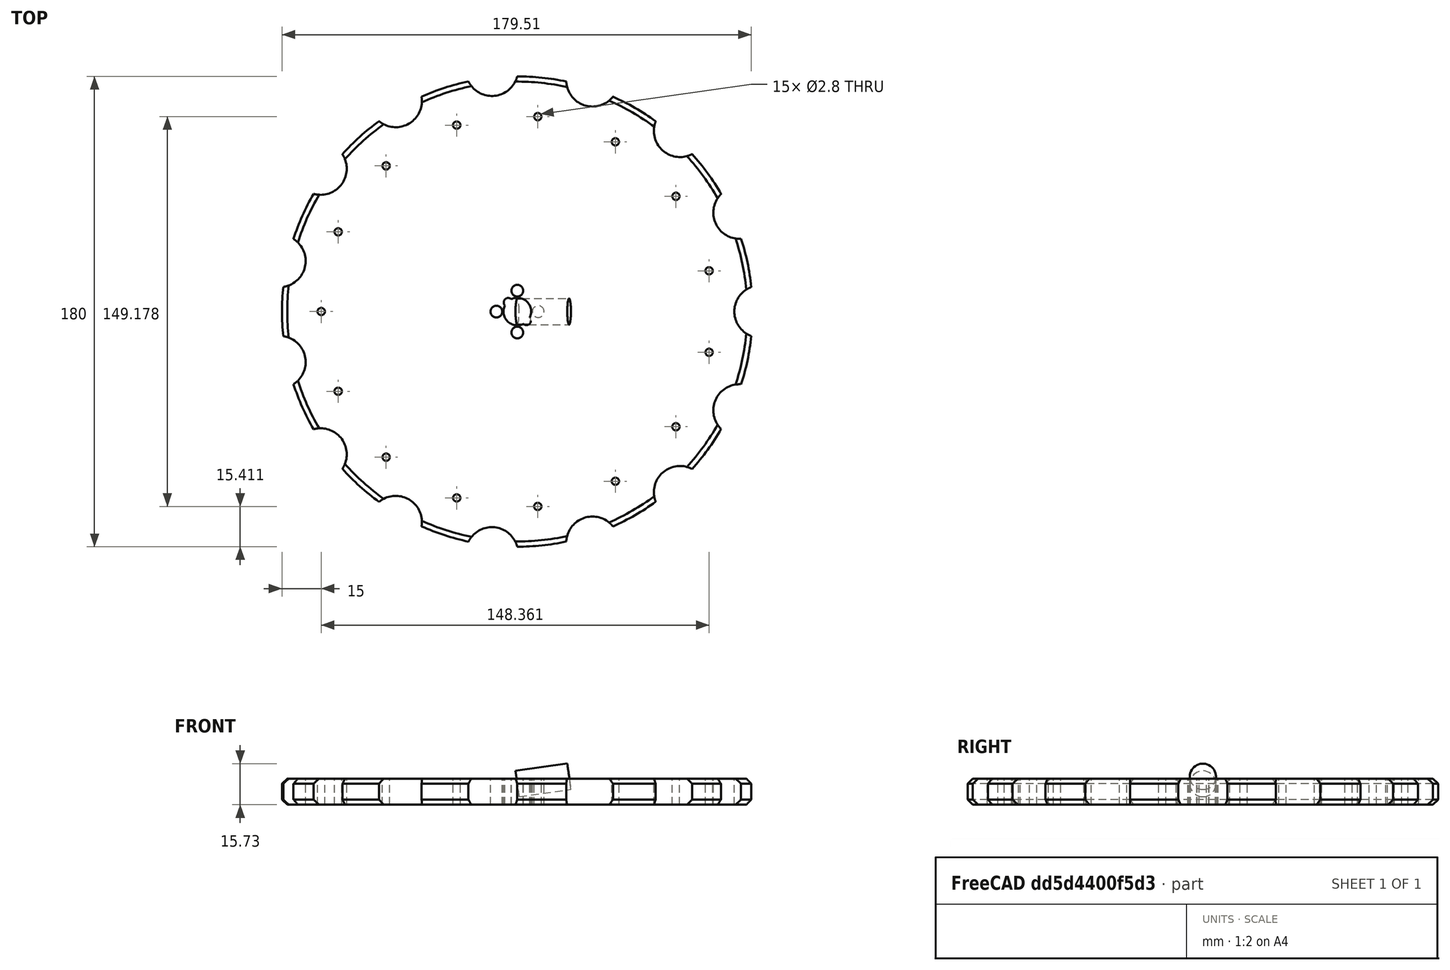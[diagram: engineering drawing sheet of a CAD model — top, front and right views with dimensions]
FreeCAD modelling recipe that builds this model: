
FCSTD DOCUMENT  (FreeCAD 0.17R13541 (Git))
Label: rueda180mmeje
License: All rights reserved
LicenseURL: http://en.wikipedia.org/wiki/All_rights_reserved
objects: Part::Cylinder×8, Part::FeaturePython×3, Part::Cut×3, Part::Chamfer×1, Part::MultiFuse×1
note: 16 computed .brp shape members not serialized (recipe doc carries the construction recipe); baked Part::Feature solids carry a one-line shape summary decoded from their .brp

FEATURE [Part::Cylinder] Cylinder  label="Cilindro"
  Angle = 360
  AttacherType = Attacher::AttachEngine3D
  Height = 10
  Radius = 90
FEATURE [Part::Chamfer] Chamfer
  Base = -> Cylinder
  Edges = 2 edges r=2: [Edge1,Edge3]
FEATURE [Part::Cylinder] Cylinder001  label="Cilindro001"
  Angle = 360
  AttacherType = Attacher::AttachEngine3D
  Height = 15
  Placement = pos=(93,0,0) rot=(0,0,1;0rad)
  Radius = 10
FEATURE [Part::FeaturePython] Array  # Draft array (typed FeaturePython)
  Angle = 360
  ArrayType = 1
  Axis = (0,0,1)
  Base = -> Cylinder001
  Center = (0,0,0)
  Fuse = false
  IntervalAxis = (0,0,0)
  IntervalX = (1,0,0)
  IntervalY = (0,1,0)
  IntervalZ = (0,0,0)
  NumberPolar = 15
  NumberX = 2
  NumberY = 2
  NumberZ = 1
FEATURE [Part::Cylinder] Cylinder004  label="Cilindro004"
  Angle = 360
  AttacherType = Attacher::AttachEngine3D
  Height = 20
  Placement = pos=(0,0,8) rot=(0,1,0;1.43117rad)
  Radius = 5
FEATURE [Part::Cylinder] Cylinder006  label="Cilindro006"
  Angle = 360
  AttacherType = Attacher::AttachEngine3D
  Height = 12
  Placement = pos=(-75,0,0) rot=(0,0,1;0rad)
  Radius = 1.4
FEATURE [Part::FeaturePython] Array001  # Draft array (typed FeaturePython)
  Angle = 360
  ArrayType = 1
  Axis = (0,0,1)
  Base = -> Cylinder006
  Center = (0,0,0)
  Fuse = false
  IntervalAxis = (0,0,0)
  IntervalX = (1,0,0)
  IntervalY = (0,1,0)
  IntervalZ = (0,0,0)
  NumberPolar = 15
  NumberX = 2
  NumberY = 2
  NumberZ = 1
FEATURE [Part::Cut] Cut
  Base = -> Chamfer
  Refine = true
  Tool = -> Array
FEATURE [Part::Cut] Cut001
  Base = -> Cut
  Refine = true
  Tool = -> Array001
FEATURE [Part::Cylinder] Cylinder007  label="Cilindro002"
  Angle = 360
  AttacherType = Attacher::AttachEngine3D
  Height = 15
  Placement = pos=(3.5,-3.5,0) rot=(0,0,1;0rad)
  Radius = 1.7
FEATURE [Part::Cylinder] Cylinder003  label="Cilindro007"
  Angle = 360
  AttacherType = Attacher::AttachEngine3D
  Height = 15
  Placement = pos=(-3.5,3.5,0) rot=(0,0,1;0rad)
  Radius = 1.7
FEATURE [Part::Cylinder] Cylinder002  label="Cilindro008"
  Angle = 360
  AttacherType = Attacher::AttachEngine3D
  Height = 15
  Placement = pos=(8,0,0) rot=(0,0,1;0rad)
  Radius = 2.25
FEATURE [Part::FeaturePython] Array002  # Draft array (typed FeaturePython)
  Angle = 360
  ArrayType = 1
  Axis = (0,0,1)
  Base = -> Cylinder002
  Center = (0,0,0)
  Fuse = false
  IntervalAxis = (0,0,0)
  IntervalX = (1,0,0)
  IntervalY = (0,1,0)
  IntervalZ = (0,0,0)
  NumberPolar = 4
  NumberX = 2
  NumberY = 2
  NumberZ = 1
FEATURE [Part::Cylinder] Cylinder008  label="eje"
  Angle = 360
  AttacherType = Attacher::AttachEngine3D
  Height = 12
  Radius = 5.3
FEATURE [Part::MultiFuse] Fusion
  Refine = true
  Shapes = -> [Cylinder003,Cylinder007,Array002,Cylinder008]
FEATURE [Part::Cut] Cut002
  Base = -> Cut001
  Refine = true
  Tool = -> Fusion
